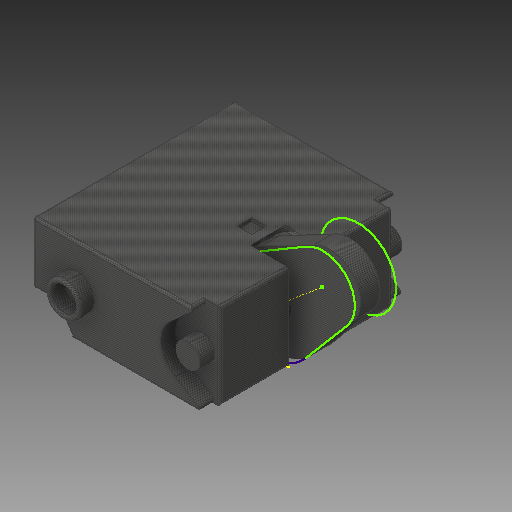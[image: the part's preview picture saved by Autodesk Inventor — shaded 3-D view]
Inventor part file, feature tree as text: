
AUTODESK INVENTOR PART (.ipt)
format: ipt  version: 2018 (Build 220112000, 112)  size: 384,000 bytes
history: native  units: mm
features: sketch x14, extrude x10, fillet x5, mirror x1, delete_face x1
ambient origin geometry x8: Origin, YZ Plane, XZ Plane, XY Plane, X Axis, Y Axis, Z Axis, Center Point
bodies: Solid1 (feature_tree), Solid2 (feature_tree)
feature tree (31):
  extrude  "Extrusion1"  Depth=30.0mm TaperAngle=0.0deg
  sketch  "Sketch2"  dims[d15=30.0mm d16=0.0mm d18=410.0mm d19=0.0mm]
  sketch  "Sketch3"  dims[d20=5.0mm d21=70.0mm d22=0.0mm]
  extrude  "Extrusion2"  Depth=410.0mm TaperAngle=0.0deg
  extrude  "Extrusion3"  Depth=70.0mm TaperAngle=0.0deg
  extrude  "Extrusion4"  Depth=70.0mm TaperAngle=0.0deg
  mirror  "Mirror1"
  fillet  "Fillet1"  Radius=5.0mm
  sketch  "Sketch7"  dims[d38=70.0mm d39=0.0mm d40=40.0mm d41=0.0mm]
  extrude  "Extrusion5"  Depth=5.0mm
  extrude  "Extrusion6"  Depth=70.0mm
  sketch  "Sketch10"
  extrude  "Extrusion7"  Depth=40.0mm TaperAngle=0.0deg
  sketch  "Sketch11"
  fillet  "Fillet2"  [1 undecoded]
  fillet  "Fillet3"  [1 undecoded]
  fillet  "Fillet4"  [1 undecoded]
  sketch  "Sketch12"
  extrude  "Extrusion8"  [1 undecoded]
  fillet  "Fillet5"  [1 undecoded]
  sketch  "Sketch13"
  extrude  "Extrusion9"  [1 undecoded]
  delete_face  "Delete Face1"
  extrude  "Extrusion10"  [1 undecoded]
  sketch  "Sketch1"  dims[d3=410.0mm d4=0.0mm d10=30.0mm d11=0.0mm]
  sketch  "Sketch4"  dims[d25=7.0mm d26=0.0mm d30=70.0mm d31=0.0mm d32=5.0mm]
  sketch  "Sketch5"  dims[d33=5.0mm d34=2.0mm]
  sketch  "Sketch6"  dims[d35=70.0mm d36=0.0mm d37=2.0mm]
  sketch  "Sketch8"
  sketch  "Sketch9"
  sketch  "Sketch14"
note: 7 required parameter values undecoded (feature->parameter linkage not recoverable at this tier; creation-order binding heuristic only, values carry confidence <= 0.55)
